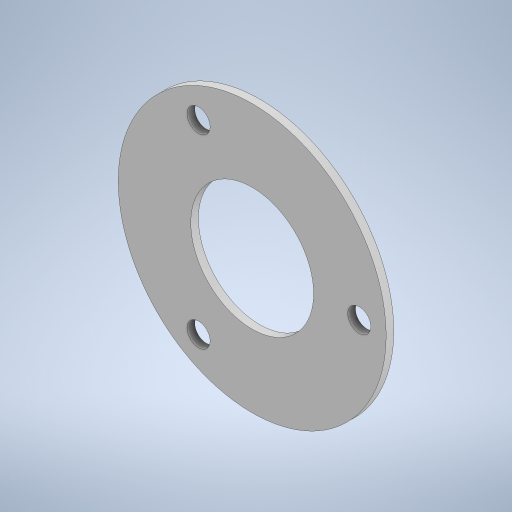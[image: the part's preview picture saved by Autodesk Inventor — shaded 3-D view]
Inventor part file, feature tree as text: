
AUTODESK INVENTOR PART (.ipt)
format: ipt  version: 2024.2 (Build 282272000, 272)  size: 276,480 bytes
history: native  units: mm
features: sketch x3, other x2, sheet_metal_op x1, hole x1, pattern_circular x1, extrude x1
ambient origin geometry x8: Origin, YZ Plane, XZ Plane, XY Plane, X Axis, Y Axis, Z Axis, Center Point
bodies: Solid1 (feature_tree)
feature tree (9):
  sheet_metal_op  "Face1"
  hole  "Hole1"  [1 undecoded]
  pattern_circular  "Circular Pattern1"  [2 undecoded]
  extrude  "Extrusion1"  Depth=2.0mm TaperAngle=360.0deg
  sketch  "Sketch1"  dims[d0=70.0mm d1=2.0mm]
  other  "Plate1"
  sketch  "Sketch2"  dims[d2=28.0mm]
  sketch  "Sketch3"  dims[d3=6.0mm d4=6.0mm d5=4.0mm d6=2.0mm d7=90.0deg d8=2.0mm d9=20.594885mm d10=30.0mm d11=360.0deg d13=32.1mm d14=0.0mm d15=0.0mm]
  other  "Definition1"
note: 3 required parameter values undecoded (feature->parameter linkage not recoverable at this tier; creation-order binding heuristic only, values carry confidence <= 0.55)
